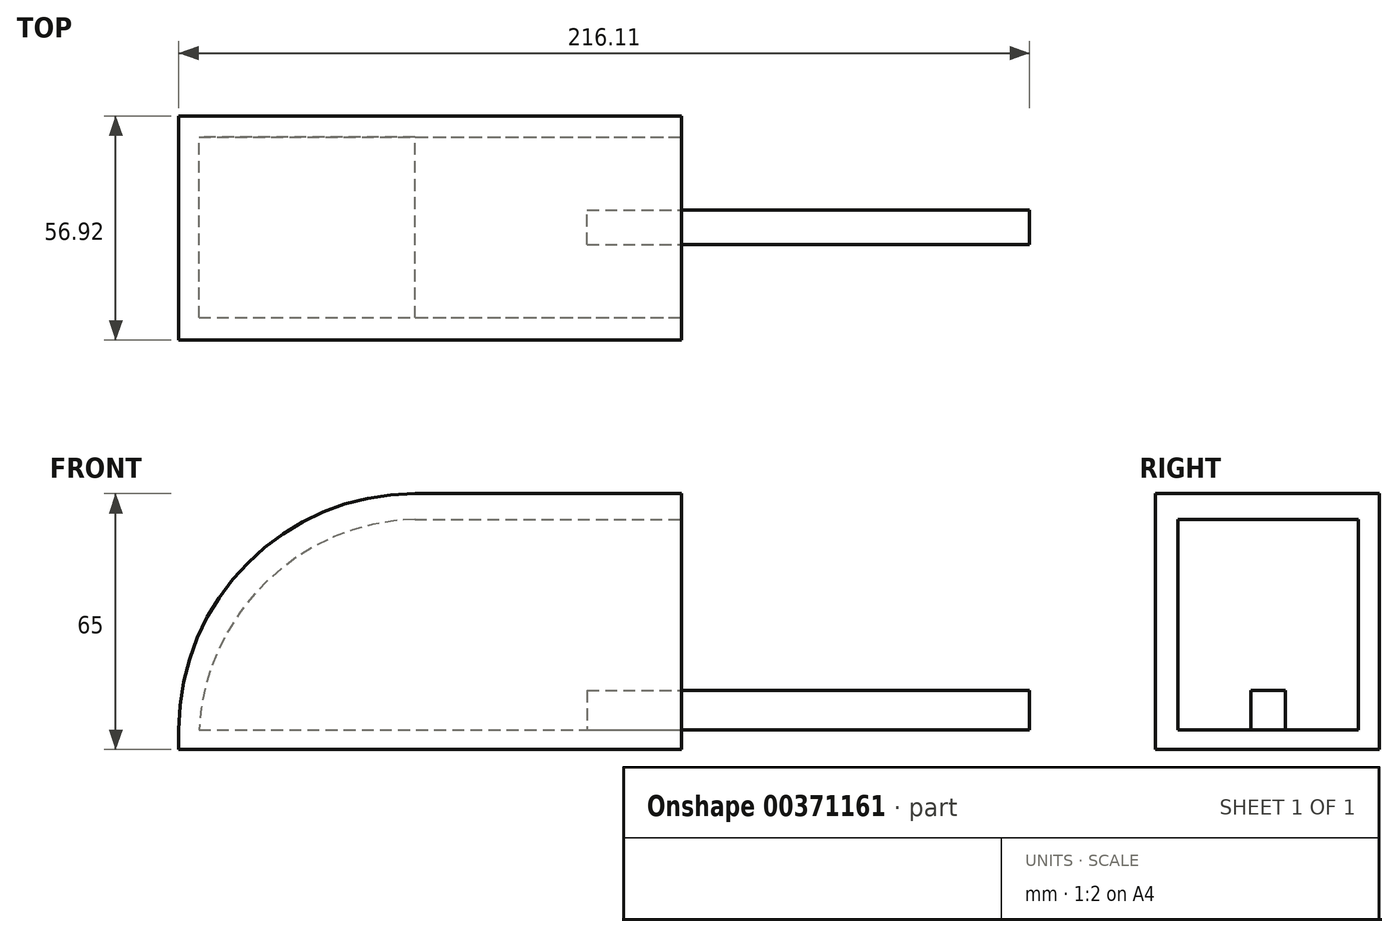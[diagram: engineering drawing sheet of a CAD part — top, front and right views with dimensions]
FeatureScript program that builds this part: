
annotation { "Feature Type Name" : "Feature", "Feature Type Description" : "" }
export const myFeature = defineFeature(function(context is Context, id is Id, definition is map)
    precondition{}
    {
        {
            var Q0;
            Q0=qCreatedBy(makeId("Top.planeOp"),FACE);
            var sketch = newSketch(context, id + "F0", { "sketchPlane" : qUnion([Q0])});
            skLineSegment(sketch, "E0.bottom", {"start": v(52.34, 51.16) * mm, "end": v(-75.38, 51.16) * mm});
            skLineSegment(sketch, "E0.top", {"start": v(52.34, -5.76) * mm, "end": v(-75.38, -5.76) * mm});
            skLineSegment(sketch, "E0.left", {"start": v(52.34, 51.16) * mm, "end": v(52.34, -5.76) * mm});
            skLineSegment(sketch, "E0.right", {"start": v(-75.38, 51.16) * mm, "end": v(-75.38, -5.76) * mm});
            skPoint(sketch, "E0.middle", {"position": v(-11.52, 22.7) * mm});
            skSolve(sketch);
        }
        {
            var Q0;
            Q0=makeQuery(id+"F0.imprint","IMPRINT",FACE,{"disambiguationData":[TD([[makeQuery(id+"F0.imprint","IMPRINT",EDGE,{"derivedFrom":sQuery(id+"F0.wireOp",EDGE,"E0.bottom")}),1.0]])]});
            extrude(context, id + "F1", {"entities" : qUnion([Q0]), "depth" : 5 * mm});
        }
        {
            var Q0;
            Q0=makeQuery(id+"F1.opExtrude","CAP_FACE",FACE,{"disambiguationData":[OSD([sQuery(id+"F0.wireOp",EDGE,"E0.bottom"),sQuery(id+"F0.wireOp",EDGE,"E0.top"),sQuery(id+"F0.wireOp",EDGE,"E0.left"),sQuery(id+"F0.wireOp",EDGE,"E0.right")])],"isStart":false});
            var sketch = newSketch(context, id + "F2", { "sketchPlane" : qUnion([Q0])});
            skLineSegment(sketch, "E1.bottom", {"start": v(-75.38, 51.16) * mm, "end": v(52.34, 51.16) * mm});
            skLineSegment(sketch, "E1.top", {"start": v(-75.38, 45.86) * mm, "end": v(52.34, 45.86) * mm});
            skLineSegment(sketch, "E1.left", {"start": v(-75.38, 51.16) * mm, "end": v(-75.38, 45.86) * mm});
            skLineSegment(sketch, "E1.right", {"start": v(52.34, 51.16) * mm, "end": v(52.34, 45.86) * mm});
            skLineSegment(sketch, "E2.bottom", {"start": v(-75.38, -5.76) * mm, "end": v(52.34, -5.76) * mm});
            skLineSegment(sketch, "E2.top", {"start": v(-75.38, -0.05) * mm, "end": v(52.34, -0.05) * mm});
            skLineSegment(sketch, "E2.left", {"start": v(-75.38, -5.76) * mm, "end": v(-75.38, -0.05) * mm});
            skLineSegment(sketch, "E2.right", {"start": v(52.34, -5.76) * mm, "end": v(52.34, -0.05) * mm});
            skLineSegment(sketch, "E3.bottom", {"start": v(28.37, 18.5) * mm, "end": v(140.73, 18.5) * mm});
            skLineSegment(sketch, "E3.top", {"start": v(28.37, 27.31) * mm, "end": v(140.73, 27.31) * mm});
            skLineSegment(sketch, "E3.left", {"start": v(28.37, 18.5) * mm, "end": v(28.37, 27.31) * mm});
            skLineSegment(sketch, "E3.right", {"start": v(140.73, 18.5) * mm, "end": v(140.73, 27.31) * mm});
            skSolve(sketch);
        }
        {
            var Q0;
            Q0 = qSketchRegion(id + "F2", true);
            extrude(context, id + "F3", {"entities" : qUnion([Q0]), "operationType" : NewBodyOperationType.ADD, "depth" : 60 * mm});
        }
        {
            var Q0;
            Q0=makeQuery(id+"F3.opExtrude","CAP_EDGE",EDGE,{"disambiguationData":[OSD([sQuery(id+"F2.wireOp",EDGE,"E1.left")])],"isStart":false});
            var Q1;
            Q1=makeQuery(id+"F3.opExtrude","CAP_EDGE",EDGE,{"disambiguationData":[OSD([sQuery(id+"F2.wireOp",EDGE,"E2.left")])],"isStart":false});
            fillet(context, id + "F4", {"entities" : qUnion([Q0, Q1]), "radius" : 60 * mm, "tangentPropagation" : true, "allowEdgeOverflow" : false});
        }
        {
            var Q0;
            Q0=makeQuery(id+"F3.opExtrude","SWEPT_FACE",FACE,{"disambiguationData":[OSD([sQuery(id+"F2.wireOp",EDGE,"E1.top")])]});
            var sketch = newSketch(context, id + "F5", { "sketchPlane" : qUnion([Q0])});
            skArc(sketch, "E4", {"start": v(-15.38, 65) * mm, "mid": v(-57.8, 47.43) * mm, "end": v(-75.38, 5) * mm});
            skArc(sketch, "E5", {"start": v(-15.38, 58.47) * mm, "mid": v(-53.28, 42.47) * mm, "end": v(-70.28, 5) * mm});
            skLineSegment(sketch, "E6", {"start": v(-15.38, 58.47) * mm, "end": v(-15.38, 65) * mm});
            skLineSegment(sketch, "E7", {"start": v(-70.28, 5) * mm, "end": v(-75.38, 5) * mm});
            skLineSegment(sketch, "E8.bottom", {"start": v(-15.38, 58.47) * mm, "end": v(52.34, 58.47) * mm});
            skLineSegment(sketch, "E8.top", {"start": v(-15.38, 65) * mm, "end": v(52.34, 65) * mm});
            skLineSegment(sketch, "E8.right", {"start": v(52.34, 58.47) * mm, "end": v(52.34, 65) * mm});
            skSolve(sketch);
        }
        {
            var Q0;
            Q0=makeQuery(id+"F5.imprint","IMPRINT",FACE,{"disambiguationData":[TD([[makeQuery(id+"F5.imprint","IMPRINT",EDGE,{"derivedFrom":sQuery(id+"F5.wireOp",EDGE,"E4")}),1.0]])]});
            extrude(context, id + "F6", {"entities" : qUnion([Q0]), "operationType" : NewBodyOperationType.ADD, "depth" : 46 * mm});
        }
        {
            var Q0;
            Q0=makeQuery(id+"F3.boolean.opBoolean","MERGE",FACE,{"derivedFrom":[makeQuery(id+"F1.opExtrude","SWEPT_FACE",FACE,{"disambiguationData":[OSD([sQuery(id+"F0.wireOp",EDGE,"E0.right")])]}),makeQuery(id+"F3.opExtrude","SWEPT_FACE",FACE,{"disambiguationData":[OSD([sQuery(id+"F2.wireOp",EDGE,"E1.left")])]}),makeQuery(id+"F3.opExtrude","SWEPT_FACE",FACE,{"disambiguationData":[OSD([sQuery(id+"F2.wireOp",EDGE,"E2.left")])]})]});
            var sketch = newSketch(context, id + "F7", { "sketchPlane" : qUnion([Q0])});
            skCircle(sketch, "E9", {"center": v(-22.7, 20.87) * mm, "radius": 8.6 * mm});
            skPoint(sketch, "E9.centerSnap0", {"position": v(-22.7, 5) * mm});
            skSolve(sketch);
        }
        {
            var Q0;
            Q0=makeQuery(id+"F7.imprint","IMPRINT",FACE,{"disambiguationData":[TD([[makeQuery(id+"F7.imprint","IMPRINT",EDGE,{"derivedFrom":sQuery(id+"F7.wireOp",EDGE,"E9")}),1.0]])]});
            extrude(context, id + "F8", {"entities" : qUnion([Q0]), "operationType" : NewBodyOperationType.REMOVE, "oppositeDirection" : true, "depth" : 20 * mm});
        }
        {
            var Q0;
            Q0 = qSketchRegion(id + "F7", true);
            extrude(context, id + "F9", {"entities" : qUnion([Q0]), "operationType" : NewBodyOperationType.REMOVE, "oppositeDirection" : true, "depth" : 25 * mm});
        }
        {
            var Q0;
            Q0=makeQuery(id+"F3.opExtrude","CAP_FACE",FACE,{"disambiguationData":[OSD([sQuery(id+"F2.wireOp",EDGE,"E3.bottom"),sQuery(id+"F2.wireOp",EDGE,"E3.top"),sQuery(id+"F2.wireOp",EDGE,"E3.left"),sQuery(id+"F2.wireOp",EDGE,"E3.right")])],"isStart":false});
            extrude(context, id + "F10", {"entities" : qUnion([Q0]), "operationType" : NewBodyOperationType.REMOVE, "oppositeDirection" : true, "depth" : 50 * mm});
        }
        {
            var Q0;
            Q0 = qSketchRegion(id + "F5", true);
            extrude(context, id + "F11", {"entities" : qUnion([Q0]), "operationType" : NewBodyOperationType.ADD, "depth" : 48 * mm});
        }
    });
